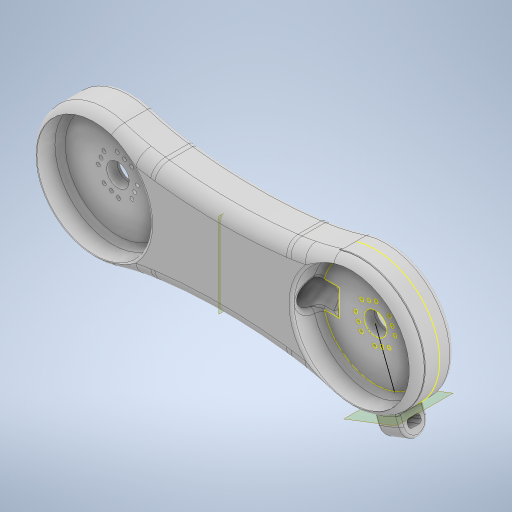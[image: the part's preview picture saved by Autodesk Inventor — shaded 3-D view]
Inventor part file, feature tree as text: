
AUTODESK INVENTOR PART (.ipt)
format: ipt  version: 2024 (Build 280153000, 153)  size: 1,906,688 bytes
history: native  units: mm
features: fillet x15, extrude x9, other x4, plane x3, projected_geometry x3, mirror x2, reference x1, sketch x1
ambient origin geometry x8: Origin, YZ Plane, XZ Plane, XY Plane, X Axis, Y Axis, Z Axis, Center Point
bodies: Solid1 (feature_tree)
feature tree (38):
  plane  "Work Plane1"
  extrude  "Extrusion1"  Depth=1.0mm TaperAngle=0.0deg
  extrude  "Extrusion2"  Depth=1.0mm
  extrude  "Extrusion3"  Depth=1.0mm TaperAngle=0.0deg
  extrude  "Extrusion4"  Depth=1.0mm
  extrude  "Extrusion5"  Depth=1.0mm
  fillet  "Fillet1"  Radius=15.0mm
  fillet  "Fillet2"  Radius=10.0mm
  fillet  "Fillet3"  Radius=20.0mm
  plane  "Work Plane3"
  mirror  "Mirror2"
  mirror  "Mirror3"
  fillet  "Fillet4"  Radius=20.0mm
  fillet  "Fillet5"  Radius=2.837941mm
  extrude  "Extrusion6"  Depth=1.0mm
  fillet  "Fillet6"  Radius=6.0mm
  fillet  "Fillet7"  Radius=10.0mm
  fillet  "Fillet10"  Radius=8.0mm
  fillet  "Fillet11"  Radius=10.0mm
  fillet  "Fillet12"  Radius=2.0mm
  fillet  "Fillet13"  Radius=2.0mm
  plane  "Work Plane5"
  extrude  "Extrusion11"  Depth=1.0mm
  extrude  "Extrusion12"  TaperAngle=0.0deg  [1 undecoded]
  extrude  "Extrusion13"  Depth=1.0mm
  fillet  "Fillet14"  Radius=100.0mm
  fillet  "Fillet15"  Radius=70.0mm
  fillet  "Fillet16"  Radius=1.0mm
  fillet  "Fillet17"  Radius=1.0mm
  reference  "Reference1"
  projected_geometry  "Projected Loop1"
  sketch  "Sketch3"  dims[d0=50.0mm d1=6.0mm d2=0.0mm d3=45.0mm d4=10.0mm d5=0.0mm d6=50.0mm d7=15.0mm d8=15.0mm d9=10.0mm d10=0.0mm d12=20.0mm d13=20.0mm d14=2.837941mm d15=12.817996mm d16=6.0mm d17=0.0mm d18=10.0mm d19=8.0mm d20=10.0mm d21=0.0mm d22=2.0mm d23=2.0mm d24=1.0mm d25=0.0mm d26=200.0mm d27=100.0mm d28=70.0mm d29=0.0mm d30=1.0mm d31=1.0mm d53=5.0mm d54=2.0mm d55=2.0mm d56=2.0mm d57=10.0mm d58=10.0mm d59=2.5mm d60=0.0mm d61=9.0mm d62=0.0mm d63=5.0mm d64=3.0mm d65=5.0mm d66=5.0mm d67=0.0mm d68=0.0mm d69=1.0mm d70=1.0mm d71=5.0mm d72=1.0mm]
  projected_geometry  "Projected Loop2"
  projected_geometry  "Projected Loop3"
  other  "<userpath> windows\Documents\Inventor\Robotska_roka\Assembly4.iam"
  other  "Assembly4.iam"
  other  "Servo Motor MG996R  With Attachments:4"
  other  "attachmentCircular_1"
note: 1 required parameter value undecoded (feature->parameter linkage not recoverable at this tier; creation-order binding heuristic only, values carry confidence <= 0.55)
